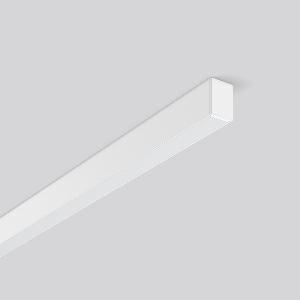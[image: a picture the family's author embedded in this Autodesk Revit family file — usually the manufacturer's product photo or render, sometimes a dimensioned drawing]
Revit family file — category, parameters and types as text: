
# Revit family: less_is_more_27_312198_002_76_3622
name_source: partatom
category: Lighting Fixtures
units: mm (PartAtom-declared; Revit-internal decimal feet)

## family parameters
Cut with Voids When Loaded = No
Host = Face
Light Source = No
Part Type = Normal
Room Calculation Point = No
Round Connector Dimension = Use Diameter
Shared = No

## types (1)
- LESS IS MORE 27 (1 x LED Modul 830, 2350 lm, 3000)
    Apparent Load = 35 VA
    CIE Flux Codes = 48 79 96 100 100
    Color Rendering = 80
    Color Temperature = 3000
    Default Elevation = 1800 mm
    Description = Series: LESS IS MORE 27
Ceiling and wall luminaire with slim design. Housing: extruded aluminium profile, powder-coated. End cap aluminium powder-coated. Diffuser made of non-yellowing plastic (PMMA), opal. Suitable for Ceiling mounting, Wall (surface). External driver with connecting cable. 
Colour: traffic white, matt (RAL 9016)
Length: 1212 mm
Width: 28 mm
Height: 38 mm
Lamp: LED
Socket: without socket
Colour temperature: 3000K
Colour rendering index (CRI): 82
System power: 35 W
Rated luminous flux: 2350 lm
Luminous efficiency: 67 lm/W
Control gear: Voltage converter, DALI dim.
Protection class: II
Type of protection: IP 20
    Height = 38 mm
    Lamp = 1 x LED Modul 830
    Lamp Light Flux = 2350 lm
    Lamp count = 1
    Length = 1212 mm
    Lifetime = 50000 h
    Luminous efficacy = 67 lm/W
    Manufacturer = RZB
    ModVariant = No
    Model = 312198.002.76
    Mounting Place = Ceiling, Wall
    Mounting Type = Surface mounted
    Number of Poles = 1
    OnlyDefault = Yes
    Power Factor = 1
    Product Name = LESS IS MORE 27
    Product group = Surface mounted LED linear luminaires
    ProductGroupID = 307
    Protection Class = Protection class II
    Protection Degree = IP 20
    RLX_Detail_Level = 1
    RLX_Emergency_Light_Flux = 0 lm
    RLX_Emergency_Type = 0
    RLX_Emergency_Type_DB = No
    RlxData = <blob elided: 22777 chars, md5=d0bca5ee>
    Socket = socket
    Standby Power = 0 W
    System Light Flux = 2350 lm
    System Power = 35 W
    Type Comments = Product without accessories
    Type Image = 312196.002.jpg
    URL = http://relux.com
    VarID = ---
    Voltage = 230 V
    Voltage Range = 220-240 V
    Weight = 0.00 kg
    Width = 28 mm

## geometry (parser evidence)
native form markers: Blend x4, Sweep x14
no freeform markers — native parametric forms only
